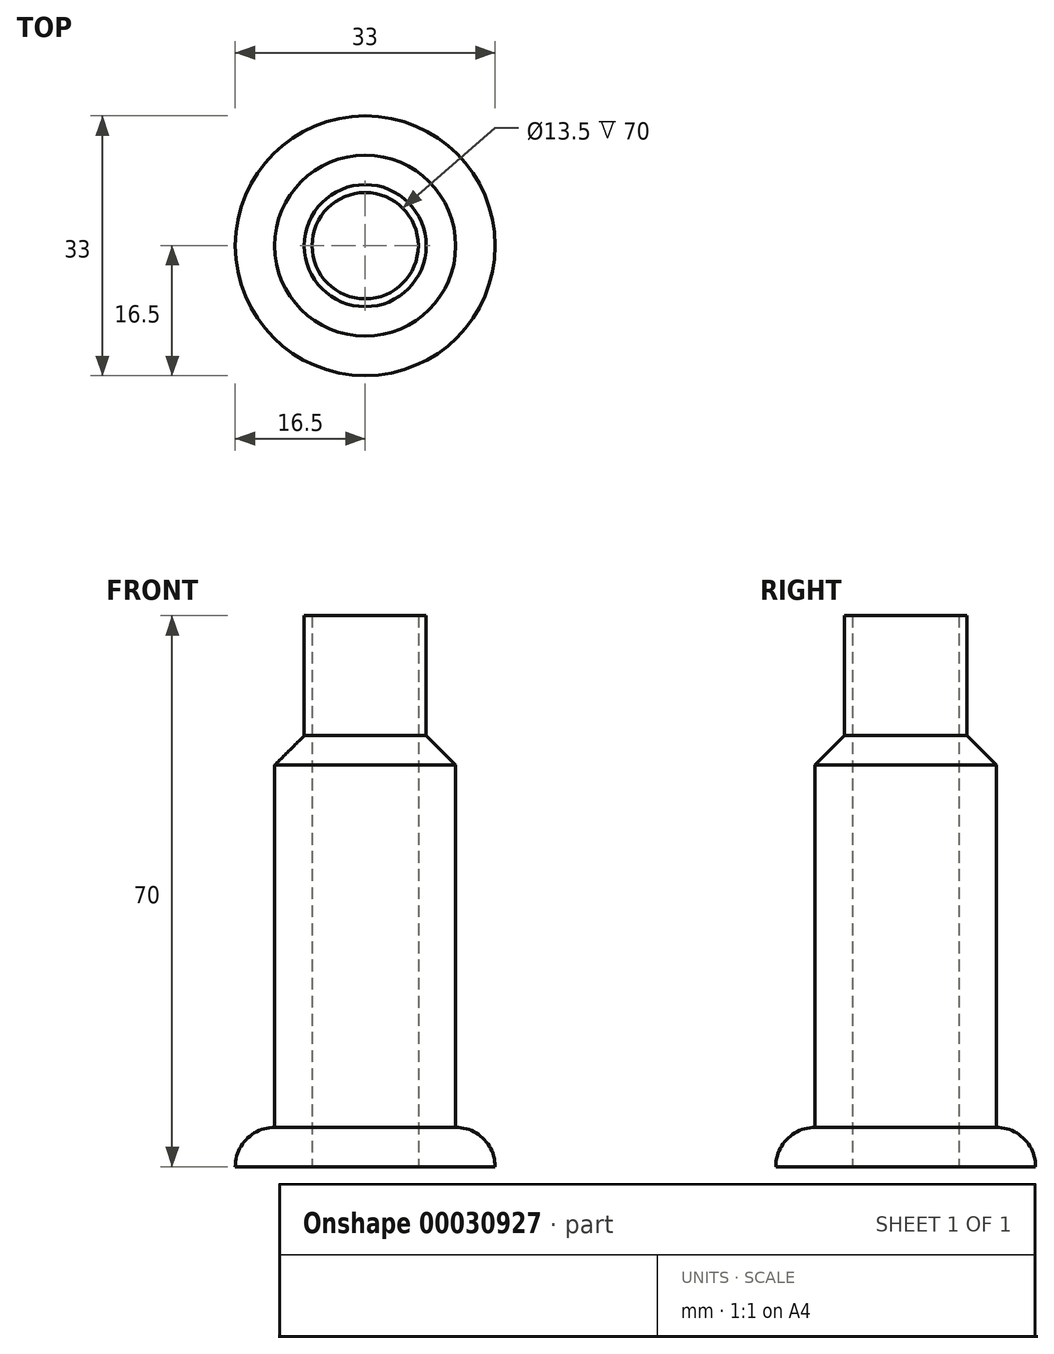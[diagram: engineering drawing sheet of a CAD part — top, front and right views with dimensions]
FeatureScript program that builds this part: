
annotation { "Feature Type Name" : "Feature", "Feature Type Description" : "" }
export const myFeature = defineFeature(function(context is Context, id is Id, definition is map)
    precondition{}
    {
        {
            var Q0;
            Q0=qCreatedBy(makeId("Top.planeOp"),FACE);
            var sketch = newSketch(context, id + "F0", { "sketchPlane" : qUnion([Q0])});
            skCircle(sketch, "E0", {"center": v(0, 0) * mm, "radius": 16.5 * mm});
            skCircle(sketch, "E1", {"center": v(0, 0) * mm, "radius": 6.75 * mm});
            skCircle(sketch, "E2", {"center": v(0, 0) * mm, "radius": 15.5 * mm});
            skCircle(sketch, "E3", {"center": v(0, 0) * mm, "radius": 7.75 * mm});
            skSolve(sketch);
        }
        {
            var Q0;
            Q0=makeQuery(id+"F0.imprint","IMPRINT",FACE,{"disambiguationData":[TD([[makeQuery(id+"F0.imprint","IMPRINT",EDGE,{"derivedFrom":sQuery(id+"F0.wireOp",EDGE,"E0")}),1.0]])]});
            var Q1;
            Q1=makeQuery(id+"F0.imprint","IMPRINT",FACE,{"disambiguationData":[TD([[makeQuery(id+"F0.imprint","IMPRINT",EDGE,{"derivedFrom":sQuery(id+"F0.wireOp",EDGE,"E2")}),1.0]])]});
            extrude(context, id + "F1", {"entities" : qUnion([Q0, Q1]), "depth" : 5 * mm});
        }
        {
            var Q0;
            Q0=makeQuery(id+"F1.opExtrude","CAP_EDGE",EDGE,{"disambiguationData":[OSD([sQuery(id+"F0.wireOp",EDGE,"E0")])],"isStart":false});
            fillet(context, id + "F2", {"entities" : qUnion([Q0]), "radius" : 5 * mm, "tangentPropagation" : true, "allowEdgeOverflow" : false});
        }
        {
            var Q0;
            Q0=makeQuery(id+"F1.opExtrude","CAP_FACE",FACE,{"disambiguationData":[OSD([sQuery(id+"F0.wireOp",EDGE,"E0"),sQuery(id+"F0.wireOp",EDGE,"E1")])],"isStart":false});
            extrude(context, id + "F3", {"entities" : qUnion([Q0]), "depth" : 51 * mm});
        }
        {
            var Q0;
            Q0=makeQuery(id+"F3.opExtrude","CAP_EDGE",EDGE,{"disambiguationData":[OSD([sQuery(id+"F0.wireOp",EDGE,"E0"),sQuery(id+"F0.wireOp",EDGE,"E1")])],"isStart":false});
            chamfer(context, id + "F4", {"entities" : qUnion([Q0]), "width" : 5 * mm, "tangentPropagation" : true});
        }
        {
            var Q0;
            Q0=makeQuery(id+"F0.imprint","IMPRINT",FACE,{"disambiguationData":[TD([[makeQuery(id+"F0.imprint","IMPRINT",EDGE,{"derivedFrom":sQuery(id+"F0.wireOp",EDGE,"E1")}),-1.0]])]});
            extrude(context, id + "F5", {"entities" : qUnion([Q0]), "operationType" : NewBodyOperationType.ADD, "depth" : 70 * mm});
        }
    });
